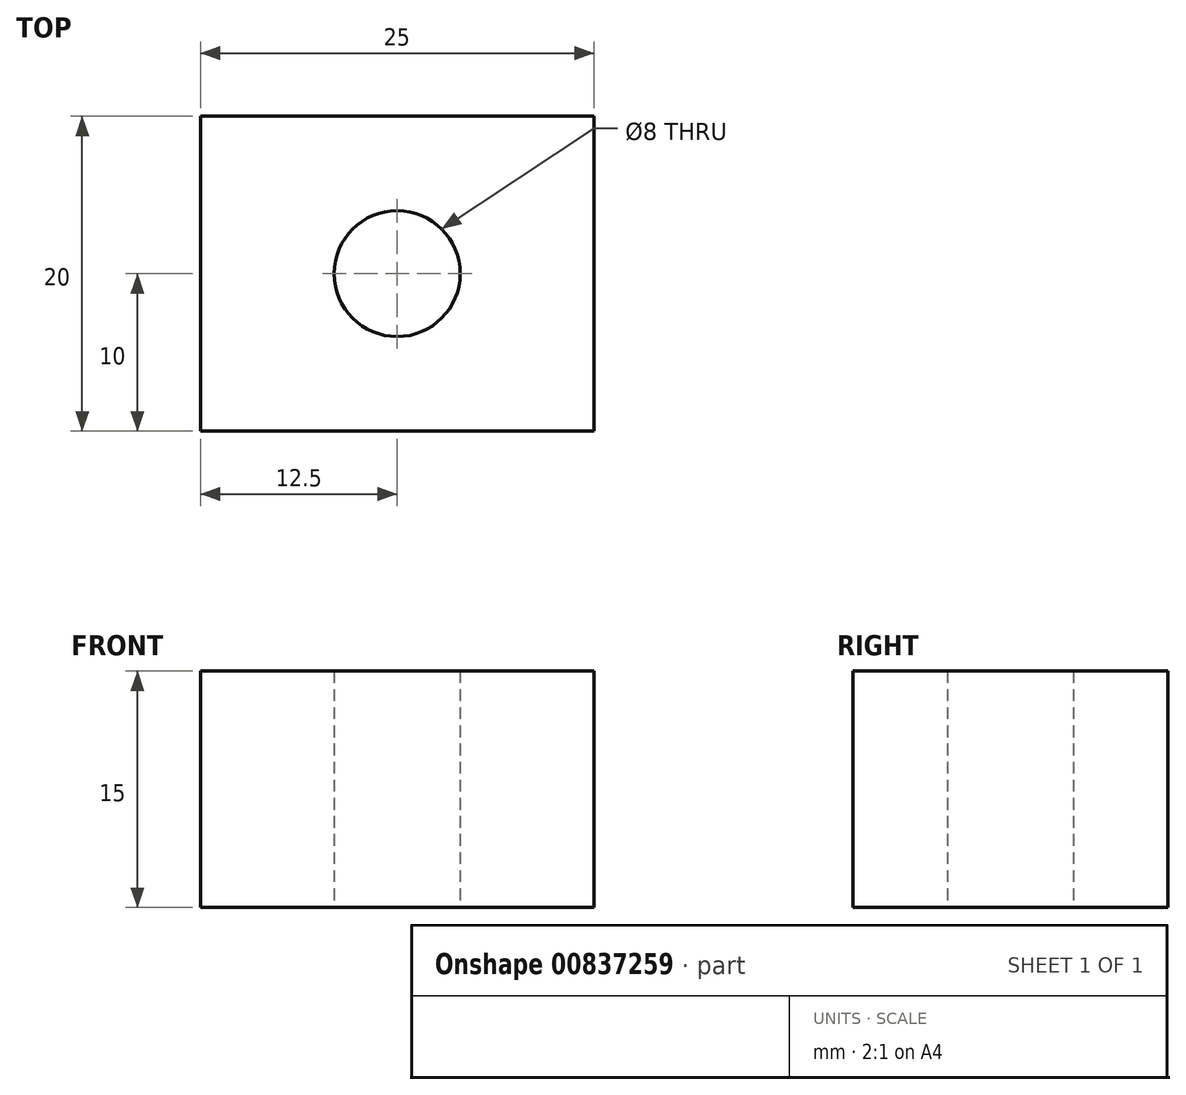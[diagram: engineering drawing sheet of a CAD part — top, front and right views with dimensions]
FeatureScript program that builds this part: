
annotation { "Feature Type Name" : "Feature", "Feature Type Description" : "" }
export const myFeature = defineFeature(function(context is Context, id is Id, definition is map)
    precondition{}
    {
        {
            var Q0;
            Q0=qCreatedBy(makeId("Top.planeOp"),FACE);
            var sketch = newSketch(context, id + "F0", { "sketchPlane" : qUnion([Q0])});
            skLineSegment(sketch, "E0.bottom", {"start": v(0, 0) * mm, "end": v(-25, 0) * mm});
            skLineSegment(sketch, "E0.top", {"start": v(0, 20) * mm, "end": v(-25, 20) * mm});
            skLineSegment(sketch, "E0.left", {"start": v(0, 0) * mm, "end": v(0, 20) * mm});
            skLineSegment(sketch, "E0.right", {"start": v(-25, 0) * mm, "end": v(-25, 20) * mm});
            skLineSegment(sketch, "E1", {"start": v(-12.5, 0) * mm, "end": v(-12.5, 20) * mm, "construction": true});
            skCircle(sketch, "E2", {"center": v(-12.5, 10) * mm, "radius": 4 * mm});
            skSolve(sketch);
        }
        {
            var Q0;
            Q0=makeQuery(id+"F0.imprint","IMPRINT",FACE,{"disambiguationData":[TD([[makeQuery(id+"F0.imprint","IMPRINT",EDGE,{"derivedFrom":sQuery(id+"F0.wireOp",EDGE,"E0.bottom")}),-1.0]])]});
            extrude(context, id + "F1", {"entities" : qUnion([Q0]), "depth" : 15 * mm, "offsetDistance" : 25.4 * mm});
        }
    });
